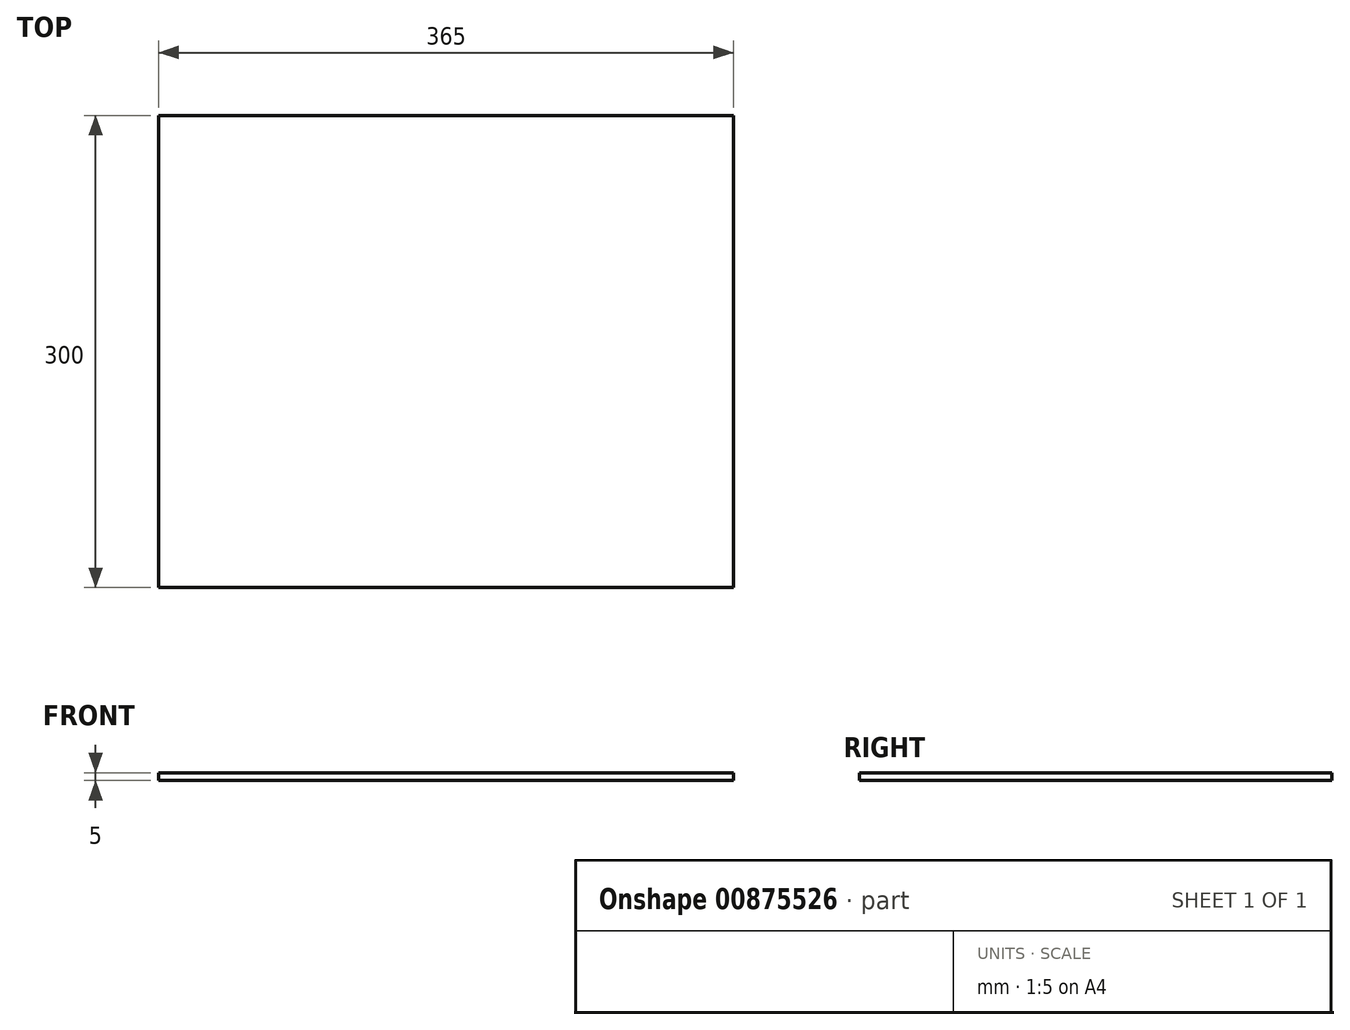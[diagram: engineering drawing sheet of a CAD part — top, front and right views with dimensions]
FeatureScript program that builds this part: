
annotation { "Feature Type Name" : "Feature", "Feature Type Description" : "" }
export const myFeature = defineFeature(function(context is Context, id is Id, definition is map)
    precondition{}
    {
        {
            var Q0;
            Q0=qCreatedBy(makeId("Top.planeOp"),FACE);
            var sketch = newSketch(context, id + "F0", { "sketchPlane" : qUnion([Q0])});
            skLineSegment(sketch, "E0.bottom", {"start": v(-198.91, -157.3) * mm, "end": v(166.09, -157.3) * mm});
            skLineSegment(sketch, "E0.top", {"start": v(-198.91, 142.7) * mm, "end": v(166.09, 142.7) * mm});
            skLineSegment(sketch, "E0.left", {"start": v(-198.91, -157.3) * mm, "end": v(-198.91, 142.7) * mm});
            skLineSegment(sketch, "E0.right", {"start": v(166.09, -157.3) * mm, "end": v(166.09, 142.7) * mm});
            skSolve(sketch);
        }
        {
            var Q0;
            Q0=makeQuery(id+"F0.imprint","IMPRINT",FACE,{"disambiguationData":[TD([[makeQuery(id+"F0.imprint","IMPRINT",EDGE,{"derivedFrom":sQuery(id+"F0.wireOp",EDGE,"E0.bottom")}),1.0]])]});
            extrude(context, id + "F1", {"entities" : qUnion([Q0]), "oppositeDirection" : true, "depth" : 5 * mm, "offsetDistance" : 25 * mm});
        }
    });
